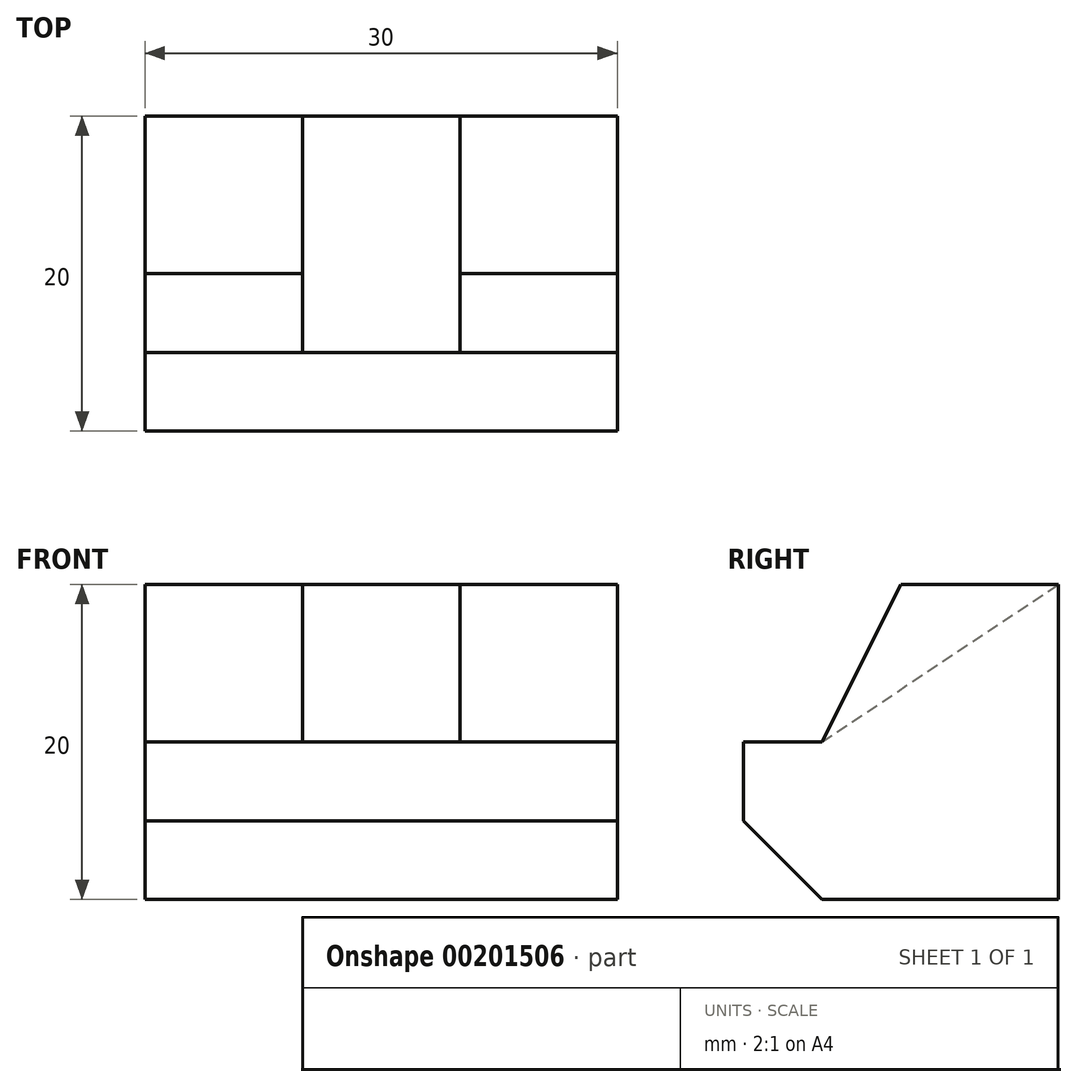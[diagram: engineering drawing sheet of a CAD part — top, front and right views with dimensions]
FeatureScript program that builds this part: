
annotation { "Feature Type Name" : "Feature", "Feature Type Description" : "" }
export const myFeature = defineFeature(function(context is Context, id is Id, definition is map)
    precondition{}
    {
        {
            var Q0;
            Q0=qCreatedBy(makeId("Right.planeOp"),FACE);
            var sketch = newSketch(context, id + "F0", { "sketchPlane" : qUnion([Q0])});
            skLineSegment(sketch, "E0", {"start": v(0, 0) * mm, "end": v(0, 20) * mm});
            skLineSegment(sketch, "E1", {"start": v(0, 20) * mm, "end": v(-10, 20) * mm});
            skLineSegment(sketch, "E2", {"start": v(-10, 20) * mm, "end": v(-15, 10) * mm});
            skLineSegment(sketch, "E3", {"start": v(-15, 10) * mm, "end": v(-20, 10) * mm});
            skLineSegment(sketch, "E4", {"start": v(-20, 10) * mm, "end": v(-20, 5) * mm});
            skLineSegment(sketch, "E5", {"start": v(-20, 5) * mm, "end": v(-15, 0) * mm});
            skLineSegment(sketch, "E6", {"start": v(-15, 0) * mm, "end": v(0, 0) * mm});
            skSolve(sketch);
        }
        {
            var Q0;
            Q0=qSketchRegion(id+"F0",true);
            extrude(context, id + "F1", {"entities" : qUnion([Q0]), "endBound" : BoundingType.SYMMETRIC, "depth" : 30 * mm});
        }
        {
            var Q0;
            Q0=qCreatedBy(makeId("Right.planeOp"),FACE);
            var sketch = newSketch(context, id + "F2", { "sketchPlane" : qUnion([Q0])});
            skLineSegment(sketch, "E7", {"start": v(-15, 10) * mm, "end": v(0, 20) * mm});
            skLineSegment(sketch, "E8", {"start": v(-15, 10) * mm, "end": v(-10, 20) * mm});
            skLineSegment(sketch, "E9", {"start": v(-10, 20) * mm, "end": v(0, 20) * mm});
            skSolve(sketch);
        }
        {
            var Q0;
            Q0=qSketchRegion(id+"F2",true);
            extrude(context, id + "F3", {"entities" : qUnion([Q0]), "operationType" : NewBodyOperationType.REMOVE, "endBound" : BoundingType.SYMMETRIC, "oppositeDirection" : true, "depth" : 10 * mm});
        }
    });
